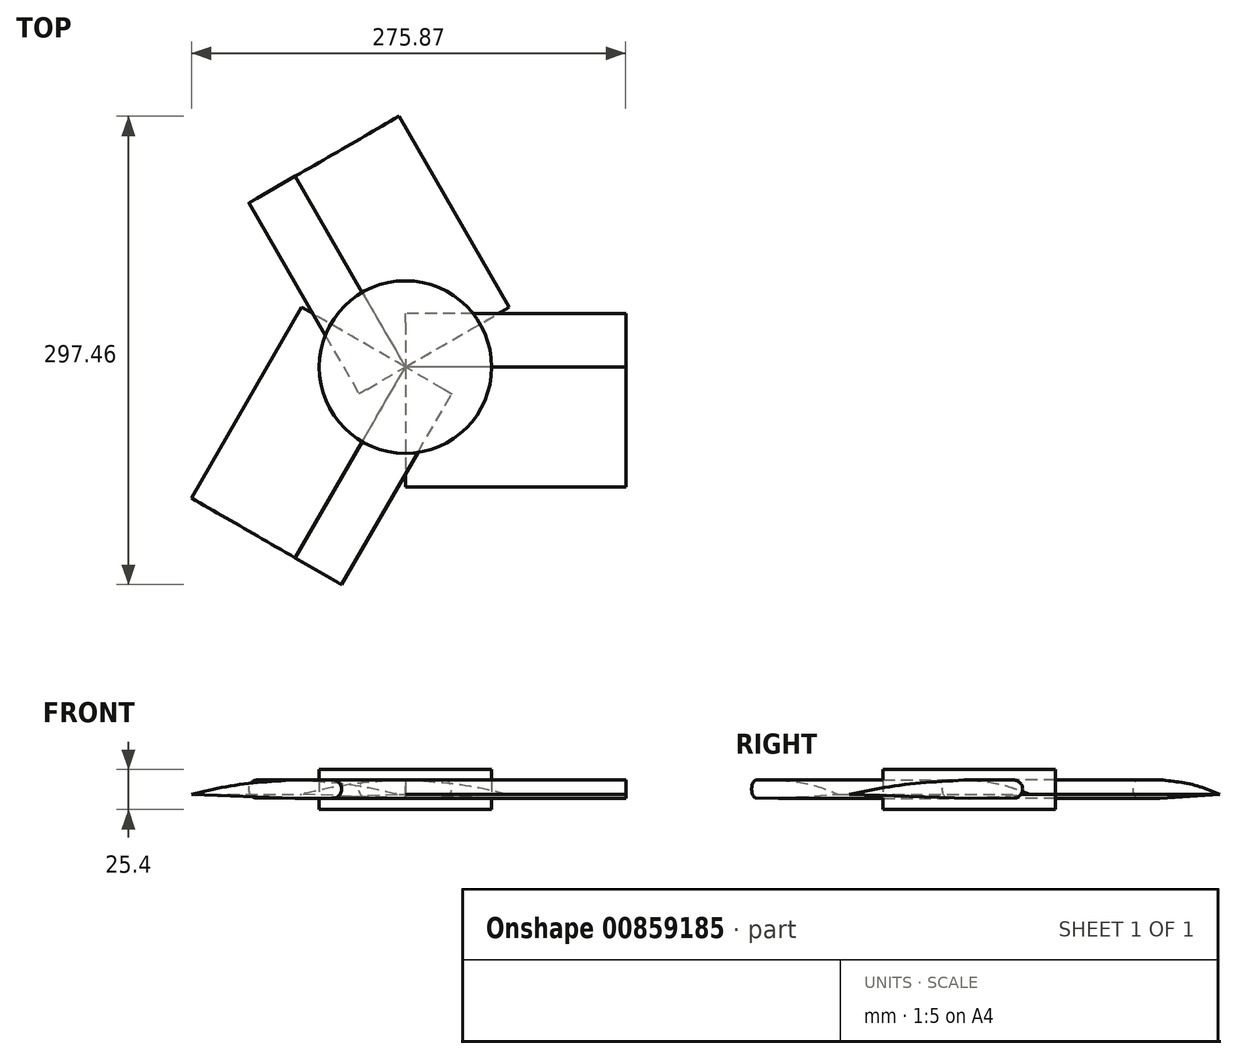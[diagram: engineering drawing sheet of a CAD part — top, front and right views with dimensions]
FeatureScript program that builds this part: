
annotation { "Feature Type Name" : "Feature", "Feature Type Description" : "" }
export const myFeature = defineFeature(function(context is Context, id is Id, definition is map)
    precondition{}
    {
        {
            var Q0;
            Q0=qCreatedBy(makeId("Right.planeOp"),FACE);
            var sketch = newSketch(context, id + "F0", { "sketchPlane" : qUnion([Q0])});
            skArc(sketch, "E0", {"start": v(28.27, -5.4) * mm, "mid": v(33.95, 0.3) * mm, "end": v(28.27, 6.02) * mm});
            skLineSegment(sketch, "E1", {"start": v(28.27, 6.02) * mm, "end": v(0, 6.18) * mm});
            skLineSegment(sketch, "E2", {"start": v(28.27, -5.4) * mm, "end": v(0, -5.56) * mm});
            skFitSpline(sketch, "E3", {"points": [v(0, 6.18) * mm, v(-40.31, 3.24) * mm, v(-76.15, -2.93) * mm], "startDerivative": vector(-79.82, -3.92) * mm, "endDerivative": vector(-72.41, -14.4) * mm});
            skLineSegment(sketch, "E4", {"start": v(0, -5.56) * mm, "end": v(-76.15, -2.93) * mm});
            skSolve(sketch);
        }
        {
            var Q0;
            Q0 = qSketchRegion(id + "F0", true);
            extrude(context, id + "F1", {"entities" : qUnion([Q0]), "depth" : 139.95 * mm, "offsetDistance" : 25.4 * mm});
        }
        {
            var Q0;
            Q0=qCreatedBy(makeId("Top.planeOp"),FACE);
            var sketch = newSketch(context, id + "F2", { "sketchPlane" : qUnion([Q0])});
            skCircle(sketch, "E5", {"center": v(0, 0) * mm, "radius": 55.6 * mm});
            skSolve(sketch);
        }
        {
            var Q0;
            Q0=makeQuery(id+"F1.opExtrude","SWEPT_BODY",BODY,{"disambiguationData":[OSD([sQuery(id+"F0.wireOp",EDGE,"E0"),sQuery(id+"F0.wireOp",EDGE,"E1"),sQuery(id+"F0.wireOp",EDGE,"E2"),sQuery(id+"F0.wireOp",EDGE,"E3"),sQuery(id+"F0.wireOp",EDGE,"E4")])]});
            var Q1;
            Q1=sQuery(id+"F2.wireOp",EDGE,"E5");
            circularPattern(context, id + "F3", {"entities" : qUnion([Q0]), "axis" : qUnion([Q1]), "angle" : 360 * degree, "instanceCount" : 3, "equalSpace" : true});
        }
        {
            var Q0;
            Q0=qCreatedBy(makeId("Top.planeOp"),FACE);
            var sketch = newSketch(context, id + "F4", { "sketchPlane" : qUnion([Q0])});
            skCircle(sketch, "E6", {"center": v(0, 0) * mm, "radius": 54.77 * mm});
            skSolve(sketch);
        }
        {
            var Q0;
            Q0 = qSketchRegion(id + "F4", true);
            extrude(context, id + "F5", {"entities" : qUnion([Q0]), "endBound" : BoundingType.SYMMETRIC, "depth" : 25.4 * mm, "offsetDistance" : 25.4 * mm});
        }
    });
